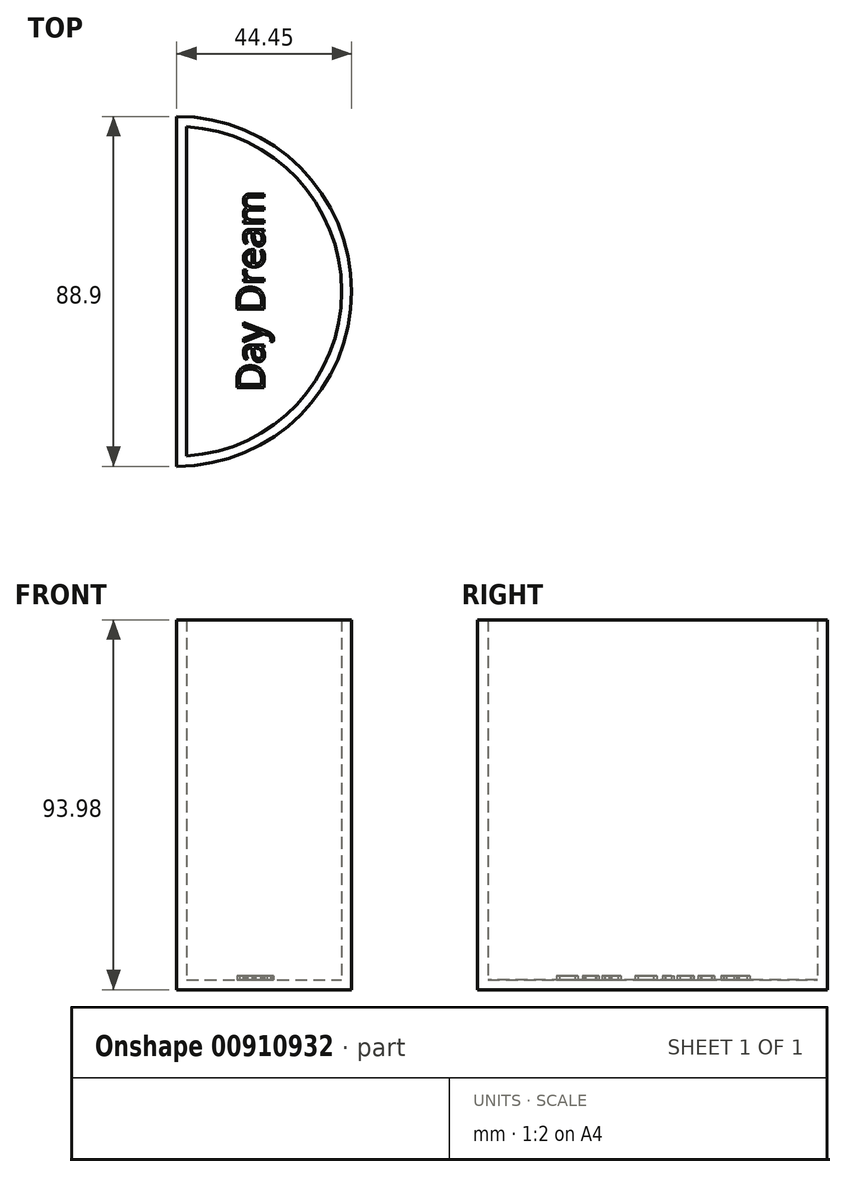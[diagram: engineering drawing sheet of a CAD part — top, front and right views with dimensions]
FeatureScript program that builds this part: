
annotation { "Feature Type Name" : "Feature", "Feature Type Description" : "" }
export const myFeature = defineFeature(function(context is Context, id is Id, definition is map)
    precondition{}
    {
        {
            var Q0;
            Q0=qCreatedBy(makeId("Top.planeOp"),FACE);
            var sketch = newSketch(context, id + "F0", { "sketchPlane" : qUnion([Q0])});
            skLineSegment(sketch, "E0", {"start": v(0, 44.45) * mm, "end": v(0, -44.45) * mm});
            skArc(sketch, "E1", {"start": v(0, -44.45) * mm, "mid": v(44.45, 0) * mm, "end": v(0, 44.45) * mm});
            skSolve(sketch);
        }
        {
            var Q0;
            Q0 = qSketchRegion(id + "F0", true);
            extrude(context, id + "F1", {"entities" : qUnion([Q0]), "depth" : 93.98 * mm, "offsetDistance" : 25.4 * mm});
        }
        {
            var Q0;
            Q0=makeQuery(id+"F1.opExtrude","CAP_FACE",FACE,{"disambiguationData":[OSD([sQuery(id+"F0.wireOp",EDGE,"E0"),sQuery(id+"F0.wireOp",EDGE,"E1")])],"isStart":false});
            shell(context, id + "F2", {"entities" : qUnion([Q0]), "thickness" : 2.54 * mm});
        }
        {
            var Q0;
            Q0=makeQuery(id+"F2.opShell","OFFSET_FACE",FACE,{"disambiguationData":[OSD([sQuery(id+"F0.wireOp",EDGE,"E0"),sQuery(id+"F0.wireOp",EDGE,"E1")])]});
            var sketch = newSketch(context, id + "F3", { "sketchPlane" : qUnion([Q0])});
            skText(sketch, "E2", { "text": "Day Dream", "fontName": "OpenSans-Regular.ttf"});
            const initialGuessF3  = {"E2": [0.02225, -0.0254, 0, 1, 0.00701]};
            skSetInitialGuess(sketch, initialGuessF3);
            skSolve(sketch);
        }
        {
            var Q0;
            Q0 = qSketchRegion(id + "F3", true);
            extrude(context, id + "F4", {"entities" : qUnion([Q0]), "operationType" : NewBodyOperationType.ADD, "depth" : 1 * mm, "offsetDistance" : 25.4 * mm});
        }
    });
